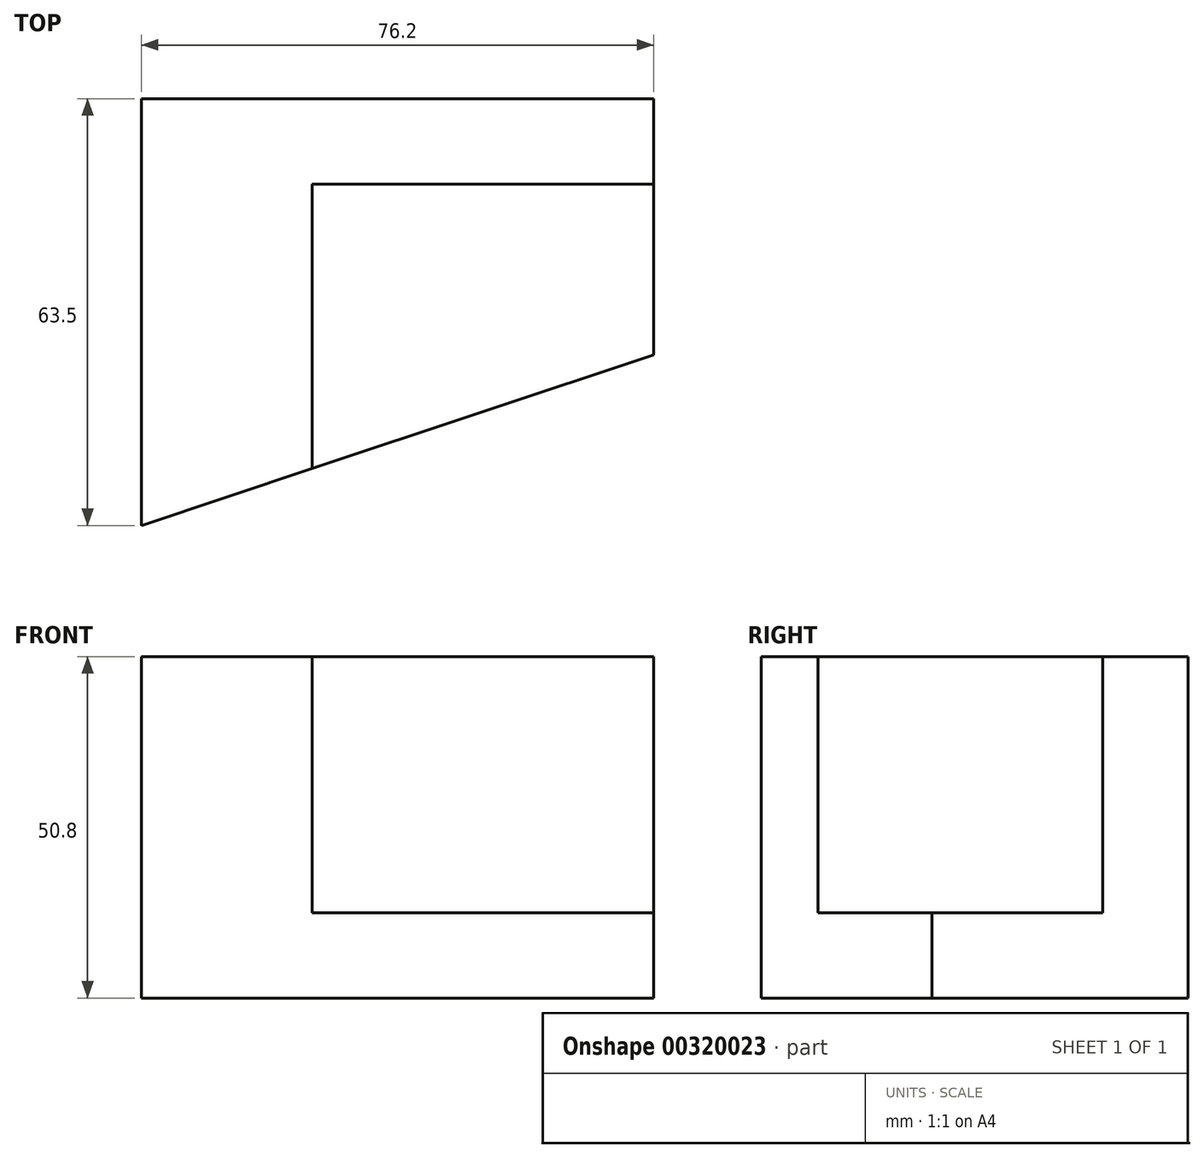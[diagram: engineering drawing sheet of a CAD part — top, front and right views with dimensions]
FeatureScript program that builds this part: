
annotation { "Feature Type Name" : "Feature", "Feature Type Description" : "" }
export const myFeature = defineFeature(function(context is Context, id is Id, definition is map)
    precondition{}
    {
        {
            var Q0;
            Q0=qCreatedBy(makeId("Front.planeOp"),FACE);
            var sketch = newSketch(context, id + "F0", { "sketchPlane" : qUnion([Q0])});
            skLineSegment(sketch, "E0", {"start": v(0, 0) * mm, "end": v(76.2, 0) * mm});
            skLineSegment(sketch, "E1", {"start": v(76.2, 0) * mm, "end": v(76.2, 50.8) * mm});
            skLineSegment(sketch, "E2", {"start": v(76.2, 50.8) * mm, "end": v(0, 50.8) * mm});
            skLineSegment(sketch, "E3", {"start": v(0, 50.8) * mm, "end": v(0, 0) * mm});
            skLineSegment(sketch, "E4", {"start": v(0, 12.7) * mm, "end": v(76.2, 12.7) * mm});
            skLineSegment(sketch, "E5", {"start": v(25.4, 50.8) * mm, "end": v(25.4, 0) * mm});
            skSolve(sketch);
        }
        {
            var Q0;
            {var subQ0=sQuery(id+"F0.wireOp",EDGE,"E2");Q0=makeQuery(id+"F0.imprint","IMPRINT",FACE,{"disambiguationData":[TD([[makeQuery(id+"F0.imprint","IMPRINT",EDGE,{"derivedFrom":subQ0}),1.0]])]});}
            extrude(context, id + "F1", {"entities" : qUnion([Q0]), "depth" : 12.7 * mm});
        }
        {
            var Q0;
            {var subQ0=sQuery(id+"F0.wireOp",EDGE,"E0");Q0=makeQuery(id+"F0.imprint","IMPRINT",FACE,{"disambiguationData":[TD([[makeQuery(id+"F0.imprint","IMPRINT",EDGE,{"derivedFrom":subQ0}),1.0]])]});}
            extrude(context, id + "F2", {"entities" : qUnion([Q0]), "operationType" : NewBodyOperationType.ADD, "depth" : 25.4 * mm});
        }
        {
            var Q0;
            {var subQ0=sQuery(id+"F0.wireOp",EDGE,"E3");var subQ1=sQuery(id+"F0.wireOp",EDGE,"E2");var subQ2=makeQuery(id+"F0.imprint","INTERSECT",VERTEX,{"derivedFrom":[subQ1,subQ0]});Q0=makeQuery(id+"F0.imprint","IMPRINT",FACE,{"disambiguationData":[TD([[makeQuery(id+"F0.imprint","IMPRINT",EDGE,{"disambiguationData":[TD([[subQ2,1.0]])],"derivedFrom":subQ1}),1.0]])]});}
            var Q1;
            {var subQ0=sQuery(id+"F0.wireOp",EDGE,"E3");var subQ1=sQuery(id+"F0.wireOp",EDGE,"E0");var subQ2=makeQuery(id+"F0.imprint","INTERSECT",VERTEX,{"derivedFrom":[subQ1,subQ0]});Q1=makeQuery(id+"F0.imprint","IMPRINT",FACE,{"disambiguationData":[TD([[makeQuery(id+"F0.imprint","IMPRINT",EDGE,{"disambiguationData":[TD([[subQ2,-1.0]])],"derivedFrom":subQ1}),1.0]])]});}
            extrude(context, id + "F3", {"entities" : qUnion([Q0, Q1]), "operationType" : NewBodyOperationType.ADD, "depth" : 63.5 * mm});
        }
        {
            var Q0;
            {var subQ0=sQuery(id+"F0.wireOp",EDGE,"E0");Q0=makeQuery(id+"F3.boolean.opBoolean","MERGE",FACE,{"derivedFrom":[makeQuery(id+"F2.opExtrude","SWEPT_FACE",FACE,{"disambiguationData":[OSD([subQ0])]}),makeQuery(id+"F3.opExtrude","SWEPT_FACE",FACE,{"disambiguationData":[OSD([subQ0])]})]});}
            var sketch = newSketch(context, id + "F4", { "sketchPlane" : qUnion([Q0])});
            skLineSegment(sketch, "E6", {"start": v(76.2, 0) * mm, "end": v(0, 0) * mm});
            skLineSegment(sketch, "E7", {"start": v(0, 0) * mm, "end": v(0, 63.5) * mm});
            skLineSegment(sketch, "E8", {"start": v(0, 63.5) * mm, "end": v(76.2, 38.1) * mm});
            skLineSegment(sketch, "E9", {"start": v(76.2, 38.1) * mm, "end": v(76.2, 0) * mm});
            skSolve(sketch);
        }
        {
            var Q0;
            {var subQ6=sQuery(id+"F4.wireOp",EDGE,"E6");Q0=makeQuery(id+"F4.imprint","IMPRINT",FACE,{"disambiguationData":[TD([[makeQuery(id+"F4.imprint","IMPRINT",EDGE,{"derivedFrom":subQ6}),1.0]])]});}
            var Q1;
            {var subQ3=sQuery(id+"F0.wireOp",EDGE,"E0");var subQ6=makeQuery(id+"F2.opExtrude","CAP_EDGE",EDGE,{"disambiguationData":[OSD([subQ3])],"isStart":false});Q1=makeQuery(id+"F4.imprint","IMPRINT",FACE,{"disambiguationData":[TD([[makeQuery(id+"F4.imprint","IMPRINT",EDGE,{"derivedFrom":subQ6}),1.0]])]});}
            extrude(context, id + "F5", {"entities" : qUnion([Q0, Q1]), "operationType" : NewBodyOperationType.ADD, "oppositeDirection" : true, "depth" : 12.7 * mm});
        }
        {
            var Q0;
            {var subQ1=sQuery(id+"F0.wireOp",EDGE,"E0");var subQ2=makeQuery(id+"F3.opExtrude","CAP_EDGE",EDGE,{"disambiguationData":[OSD([subQ1])],"isStart":false});Q0=makeQuery(id+"F4.imprint","IMPRINT",FACE,{"disambiguationData":[TD([[makeQuery(id+"F4.imprint","IMPRINT",EDGE,{"derivedFrom":subQ2}),-1.0]])]});}
            var Q1;
            {var subQ0=sQuery(id+"F0.wireOp",EDGE,"E2");Q1=makeQuery(id+"F3.boolean.opBoolean","MERGE",FACE,{"derivedFrom":[makeQuery(id+"F1.opExtrude","SWEPT_FACE",FACE,{"disambiguationData":[OSD([subQ0])]}),makeQuery(id+"F3.opExtrude","SWEPT_FACE",FACE,{"disambiguationData":[OSD([subQ0])]})]});}
            extrude(context, id + "F6", {"entities" : qUnion([Q0]), "operationType" : NewBodyOperationType.REMOVE, "endBound" : BoundingType.UP_TO_SURFACE, "oppositeDirection" : true, "endBoundEntityFace" : qUnion([Q1]), "depth" : 25.4 * mm});
        }
    });
